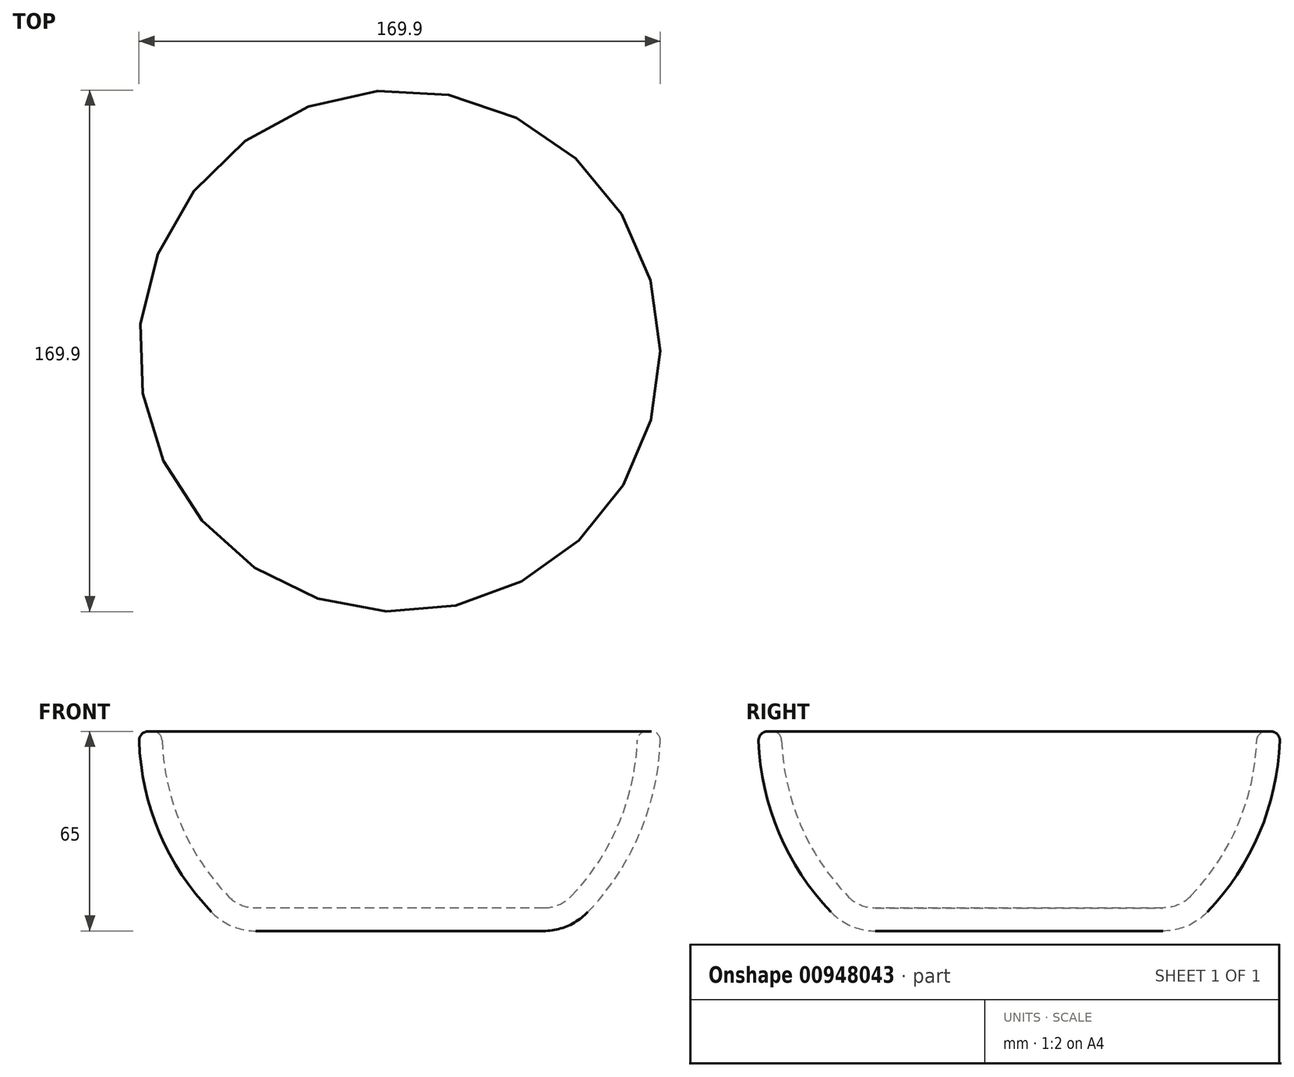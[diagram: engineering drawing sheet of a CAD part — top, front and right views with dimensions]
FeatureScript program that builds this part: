
annotation { "Feature Type Name" : "Feature", "Feature Type Description" : "" }
export const myFeature = defineFeature(function(context is Context, id is Id, definition is map)
    precondition{}
    {
        {
            var Q0;
            Q0=qCreatedBy(makeId("Top.planeOp"),FACE);
            var sketch = newSketch(context, id + "F0", { "sketchPlane" : qUnion([Q0])});
            skCircle(sketch, "E0", {"center": v(0, 0) * mm, "radius": 85 * mm});
            skSolve(sketch);
        }
        {
            var Q0;
            Q0 = qSketchRegion(id + "F0", true);
            extrude(context, id + "F1", {"entities" : qUnion([Q0]), "depth" : 85 * mm, "offsetDistance" : 25 * mm});
        }
        {
            var Q0;
            Q0=makeQuery(id+"F1.opExtrude","CAP_EDGE",EDGE,{"disambiguationData":[OSD([sQuery(id+"F0.wireOp",EDGE,"E0")])],"isStart":true});
            fillet(context, id + "F2", {"entities" : qUnion([Q0]), "radius" : 85 * mm, "tangentPropagation" : true, "allowEdgeOverflow" : false});
        }
        {
            var Q0;
            Q0=qCreatedBy(makeId("Top.planeOp"),FACE);
            var sketch = newSketch(context, id + "F3", { "sketchPlane" : qUnion([Q0])});
            skLineSegment(sketch, "E1.bottom", {"start": v(-74.8, 75.03) * mm, "end": v(75.24, 75.03) * mm});
            skLineSegment(sketch, "E1.top", {"start": v(-74.8, -75.46) * mm, "end": v(75.24, -75.46) * mm});
            skLineSegment(sketch, "E1.left", {"start": v(-74.8, 75.03) * mm, "end": v(-74.8, -75.46) * mm});
            skLineSegment(sketch, "E1.right", {"start": v(75.24, 75.03) * mm, "end": v(75.24, -75.46) * mm});
            skSolve(sketch);
        }
        {
            var Q0;
            Q0 = qSketchRegion(id + "F3", true);
            extrude(context, id + "F4", {"entities" : qUnion([Q0]), "operationType" : NewBodyOperationType.REMOVE, "depth" : 20 * mm, "offsetDistance" : 25 * mm});
        }
        {
            var Q0;
            Q0=makeQuery(id+"F4.boolean.opBoolean","INTERSECT",EDGE,{"derivedFrom":[makeQuery(id+"F2.opFillet","BLEND_FACE",FACE,{"disambiguationData":[OSD([sQuery(id+"F0.wireOp",EDGE,"E0")])]}),makeQuery(id+"F4.opExtrude","CAP_FACE",FACE,{"disambiguationData":[OSD([sQuery(id+"F3.wireOp",EDGE,"E1.bottom"),sQuery(id+"F3.wireOp",EDGE,"E1.top"),sQuery(id+"F3.wireOp",EDGE,"E1.left"),sQuery(id+"F3.wireOp",EDGE,"E1.right")])],"isStart":false})]});
            fillet(context, id + "F5", {"entities" : qUnion([Q0]), "radius" : 20 * mm, "tangentPropagation" : true, "allowEdgeOverflow" : false});
        }
        {
            var Q0;
            Q0=makeQuery(id+"F1.opExtrude","CAP_FACE",FACE,{"disambiguationData":[OSD([sQuery(id+"F0.wireOp",EDGE,"E0")])],"isStart":false});
            shell(context, id + "F6", {"entities" : qUnion([Q0]), "thickness" : 7.5 * mm});
        }
        {
            var Q0;
            {var subQ0=sQuery(id+"F0.wireOp",EDGE,"E0");Q0=makeQuery(id+"F2.opFillet","BLEND_EDGE",EDGE,{"blendedFrom":[makeQuery(id+"F1.opExtrude","CAP_EDGE",EDGE,{"disambiguationData":[OSD([subQ0])],"isStart":true}),makeQuery(id+"F1.opExtrude","CAP_FACE",FACE,{"disambiguationData":[OSD([subQ0])],"isStart":false})],"blendedInto":[makeQuery(id+"F1.opExtrude","CAP_FACE",FACE,{"disambiguationData":[OSD([subQ0])],"isStart":false})]});}
            var Q1;
            Q1=makeQuery(id+"F6.opShell","OFFSET_EDGE",EDGE,{"disambiguationData":[OSD([sQuery(id+"F0.wireOp",EDGE,"E0")])]});
            fillet(context, id + "F7", {"entities" : qUnion([Q0, Q1]), "radius" : 3 * mm, "tangentPropagation" : true, "allowEdgeOverflow" : false});
        }
    });
